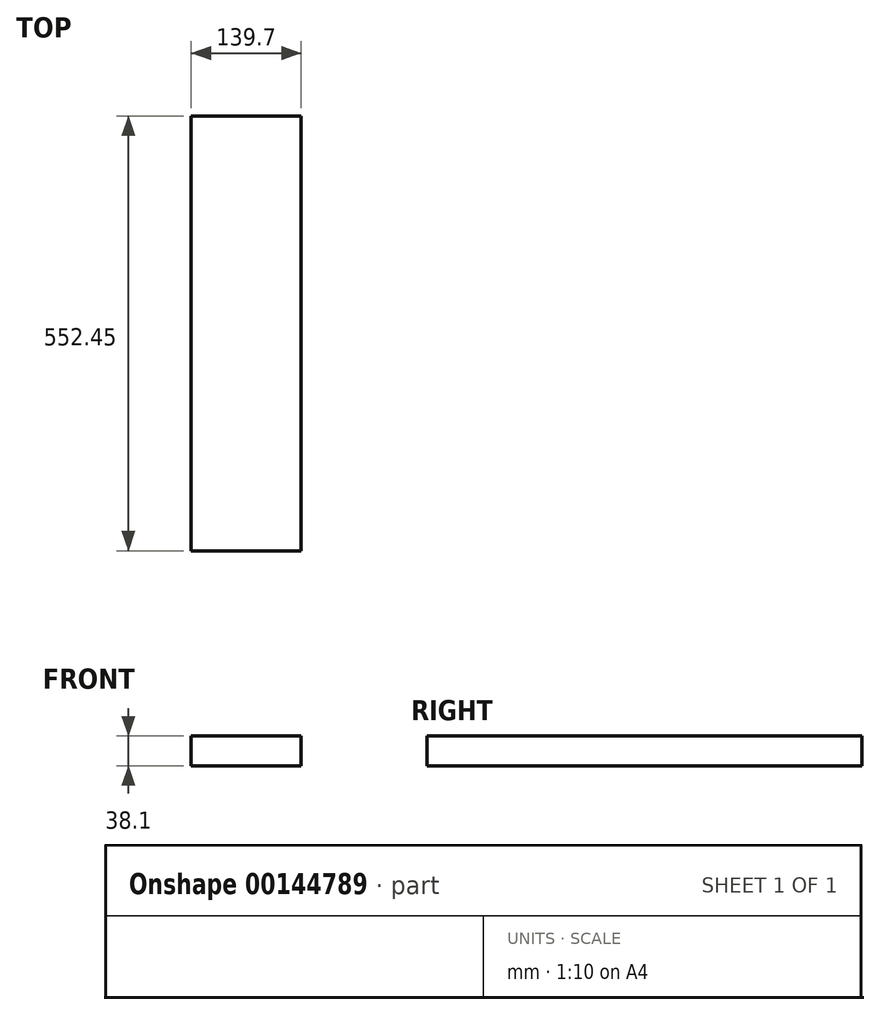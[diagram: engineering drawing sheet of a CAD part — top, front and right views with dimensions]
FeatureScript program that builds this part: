
annotation { "Feature Type Name" : "Feature", "Feature Type Description" : "" }
export const myFeature = defineFeature(function(context is Context, id is Id, definition is map)
    precondition{}
    {
        {
            var Q0;
            Q0=qCreatedBy(makeId("Front.planeOp"),FACE);
            var sketch = newSketch(context, id + "F0", { "sketchPlane" : qUnion([Q0])});
            skLineSegment(sketch, "E0.bottom", {"start": v(0, 0) * mm, "end": v(139.7, 0) * mm});
            skLineSegment(sketch, "E0.top", {"start": v(0, 38.1) * mm, "end": v(139.7, 38.1) * mm});
            skLineSegment(sketch, "E0.left", {"start": v(0, 0) * mm, "end": v(0, 38.1) * mm});
            skLineSegment(sketch, "E0.right", {"start": v(139.7, 0) * mm, "end": v(139.7, 38.1) * mm});
            skSolve(sketch);
        }
        {
            var Q0;
            Q0=makeQuery(id+"F0.imprint","IMPRINT",FACE,{"disambiguationData":[TD([[makeQuery(id+"F0.imprint","IMPRINT",EDGE,{"derivedFrom":sQuery(id+"F0.wireOp",EDGE,"E0.bottom")}),1.0]])]});
            extrude(context, id + "F1", {"entities" : qUnion([Q0]), "depth" : 552.45 * mm});
        }
    });
